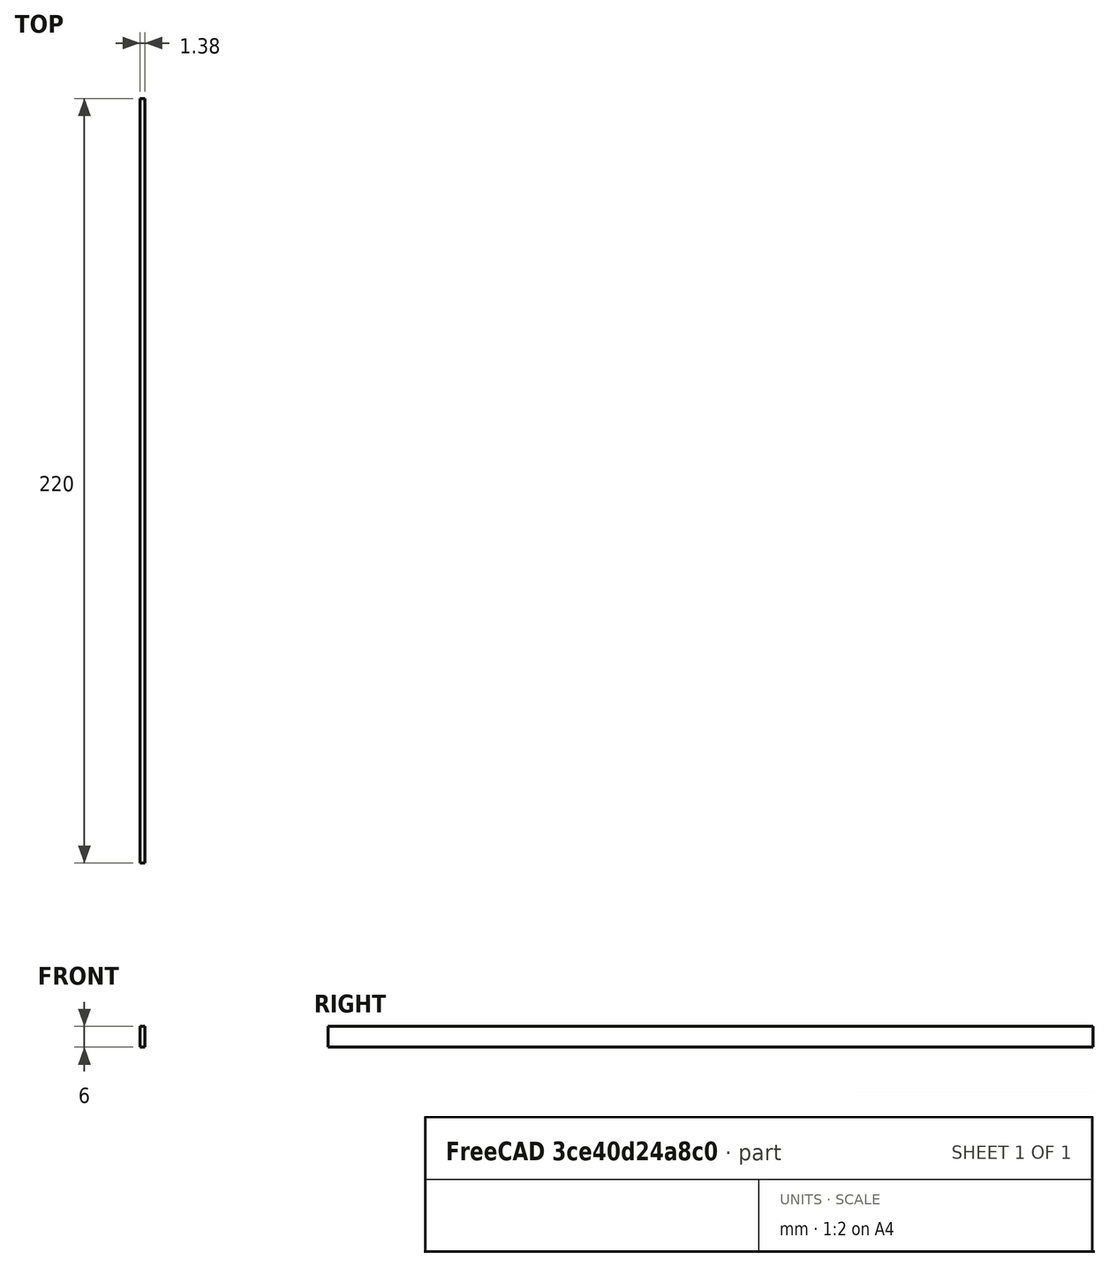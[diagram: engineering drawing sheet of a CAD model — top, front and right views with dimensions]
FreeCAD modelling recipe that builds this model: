
FCSTD DOCUMENT  (FreeCAD 0.20R27078 (Git))
Label: belt 220 mm
License: All rights reserved
LicenseURL: http://en.wikipedia.org/wiki/All_rights_reserved
objects: Sketcher::SketchObject×1, PartDesign::Pad×1, PartDesign::Body×1
note: 4 computed .brp shape members not serialized (recipe doc carries the construction recipe); baked Part::Feature solids carry a one-line shape summary decoded from their .brp

FEATURE [Sketcher::SketchObject] Sketch005
  FullyConstrained = true
  MapMode = 5
  Placement = pos=(0,0,0) rot=(1,0,0;1.5708rad)
  Support = -> [XZ_Plane003]
  sketch-geometry (4):
    g0: LineSegment StartX=0 StartY=6 StartZ=0 EndX=1.38 EndY=6 EndZ=0
    g1: LineSegment StartX=1.38 StartY=6 StartZ=0 EndX=1.38 EndY=0 EndZ=0
    g2: LineSegment StartX=1.38 StartY=0 StartZ=0 EndX=0 EndY=0 EndZ=0
    g3: LineSegment StartX=0 StartY=0 StartZ=0 EndX=0 EndY=6 EndZ=0
  constraints (12):
    c: Coincident(g0,g1)
    c: Coincident(g1,g2)
    c: Coincident(g2,g3)
    c: Coincident(g3,g0)
    c: Horizontal(g0)
    c: Horizontal(g2)
    c: Vertical(g1)
    c: Vertical(g3)
    c: PointOnObject(g0,g-2)
    c: PointOnObject(g1,g-1)
    c: DistanceY(g3,g3) = 6
    c: DistanceX(g0,g0) = 1.38
FEATURE [PartDesign::Pad] Pad001
  Direction = (0,-1,-2e-16)
  Length = 220
  Length2 = 100
  Placement = pos=(0,0,0) rot=(1,0,0;1.5708rad)
  Profile = -> Sketch005
  ReferenceAxis = -> Sketch005 [N_Axis]
  Type = 0
FEATURE [PartDesign::Body] Body003  label="belt 220 mm"
  Group = -> [Sketch005,Pad001]
  Origin = -> Origin003
  Tip = -> Pad001
